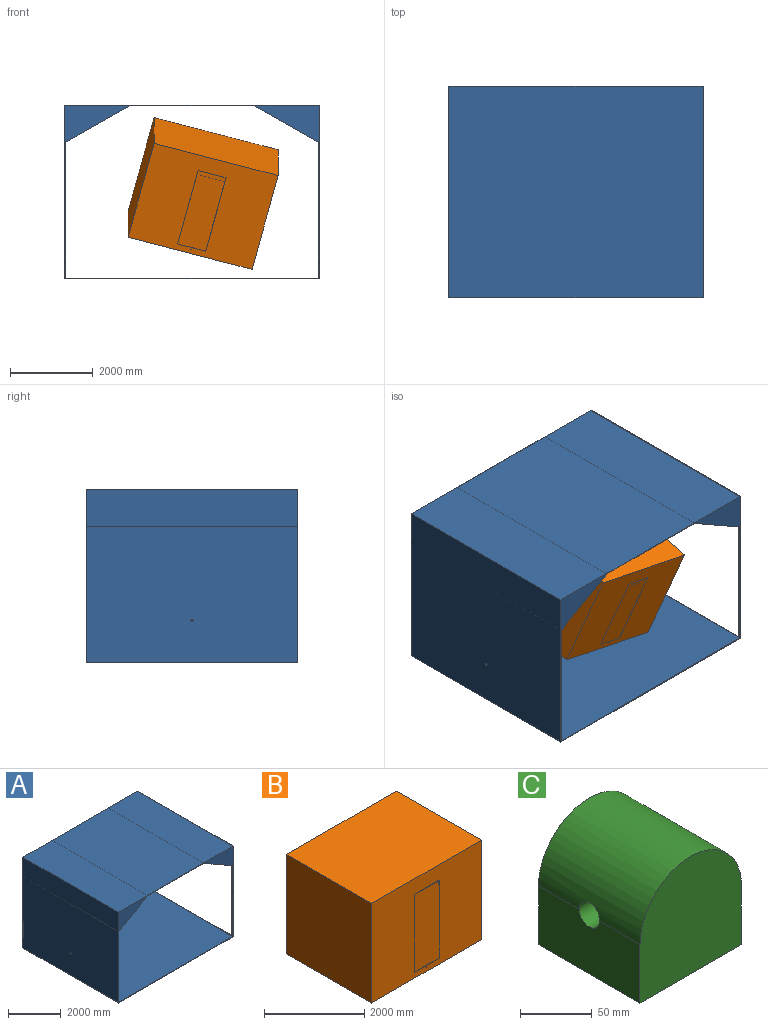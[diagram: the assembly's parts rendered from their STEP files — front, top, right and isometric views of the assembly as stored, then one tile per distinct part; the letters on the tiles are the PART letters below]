
ASSEMBLY  parts=3 mates=2
PART A: 20 faces, bbox 6140x5100x4200 mm
  f0: plane 5100x3000mm, normal (0,0,-1), area 15300000mm2, adj f10,f11,f17,f19
  f1: plane 3280x55mm, normal (-1,0,0), area 180400mm2, adj f7,f10,f12,f19
  f2: plane 5100x4200mm, normal (1,0,0), area 656610mm2, adj f3,f5,f9,f10,f11,f12,f13,f16
  f3: plane 6140x5100mm, normal (0,0,1), area 31314000mm2, adj f2,f4,f10,f11
  f4: plane 5100x4200mm, normal (-1,0,0), area 21418036.5mm2, adj f3,f9,f10,f11,f14
  f5: plane 4990x20mm, normal (0,0,-1), area 99800mm2, adj f2,f12,f13,f18
  f6: plane 3280x55mm, normal (-1,0,0), area 180400mm2, adj f7,f11,f13,f19
  f7: plane 6100x5100mm, normal (0,0,1), area 31110000mm2, adj f1,f6,f8,f10,f11,f15
  f8: plane 5100x3280mm, normal (1,0,0), area 16726036.5mm2, adj f7,f10,f11,f14,f17
  f9: plane 6140x5100mm, normal (0,0,-1), area 31314000mm2, adj f2,f4,f10,f11
  f10: plane 6140x4200mm, normal (0,-1,0), area 1776000mm2, adj f0,f1,f2,f3,f4,f7,f8,f9
  f11: plane 6140x4200mm, normal (0,1,0), area 1776000mm2, adj f0,f2,f3,f4,f6,f7,f8,f9
  f12: plane 4161x20mm, normal (0,1,0), area 83220mm2, adj f1,f2,f5,f15,f16,f18
  f13: plane 4161x20mm, normal (0,-1,0), area 83220mm2, adj f2,f5,f6,f15,f16,f18
  f14: cylinder r=25mm len=50mm, axis (1,0,0), area 3141.6mm2, adj f4,f8
  f15: plane 4990x1mm, normal (1,0,0), area 4990mm2, adj f7,f12,f13,f16
  f16: plane 4990x20mm, normal (0,0,1), area 99800mm2, adj f2,f12,f13,f15
  f17: plane 5100x1550mm, normal (0.49,0,-0.87), area 9090168.8mm2, adj f0,f8,f10,f11
  f18: plane 4990x880mm, normal (1,0,0), area 4391200mm2, adj f5,f12,f13,f19
  f19: plane 5100x1550mm, normal (-0.49,0,-0.87), area 9090168.8mm2, adj f0,f1,f6,f10,f11,f18
PART B: 68 faces, bbox 3100x2406.1x2445 mm
  f0: plane 700x20mm, normal (0,0,1), area 2139.3mm2, adj f1,f61,f62,f63,f65
  f1: plane 3100x2430mm, normal (0,-1,0), area 6202770.4mm2, adj f0,f2,f21,f22,f23,f24,f55,f61
  f2: plane 700x20mm, normal (0,0,-1), area 2139.3mm2, adj f1,f61,f62,f63,f65
  f3: plane 754.5x754.5mm, normal (0,0,-1), area 493317.8mm2, adj f12,f26,f29,f39,f40,f41,f42,f54
  f4: plane 754.5x754.5mm, normal (0,0,-1), area 527455.2mm2, adj f5,f7,f9,f12,f14,f15,f26,f27
  f5: cylinder r=7.5mm len=11.36mm, axis (0,0,-1), area 12.7mm2, adj f4,f6,f55
  f6: plane 11.36x2.6mm, normal (0,0,-1), area 20.5mm2, adj f5,f55
  f7: plane 195.1x1mm, normal (0,1,0), area 195mm2, adj f4,f10,f32,f55
  f8: cylinder r=7.5mm len=11.36mm, axis (0,0,-1), area 12.7mm2, adj f10,f11,f55
  f9: plane 195.1x1mm, normal (0,-1,0), area 195mm2, adj f4,f10,f32,f55
  f10: plane 200x195.1mm, normal (0,0,-1), area 38999.7mm2, adj f7,f8,f9,f32,f55
  f11: plane 11.18x2.5mm, normal (0,0,-1), area 19.4mm2, adj f8,f55
  f12: cylinder r=5mm len=1550mm, axis (-1,0,0), area 36462.4mm2, adj f3,f4,f14,f15,f16,f21,f26,f39
  f13: plane 754.5x754.5mm, normal (0,0,-1), area 493317.8mm2, adj f17,f28,f29,f45,f47,f48,f53,f54
  f14: plane 85.4x49.31mm, normal (-0.5,0.87,0), area 98.5mm2, adj f4,f12,f15,f44
  f15: plane 49.31x28.47mm, normal (0.87,0.5,0), area 56.9mm2, adj f4,f12,f14,f44
  f16: plane 387.31x373.21mm, normal (0,0,-1), area 75789.6mm2, adj f12,f39,f40,f41,f42,f43
  f17: plane 287.31x165.88mm, normal (-0.87,0.5,0), area 331.7mm2, adj f13,f19,f45,f53
  f18: plane 85.4x49.31mm, normal (0.5,0.87,0), area 98.5mm2, adj f20,f46,f50,f53
  f19: plane 387.31x373.21mm, normal (0,0,-1), area 75789.6mm2, adj f17,f45,f47,f48,f49,f53
  f20: plane 754.5x754.5mm, normal (0,0,-1), area 527455.2mm2, adj f18,f27,f28,f30,f33,f34,f36,f46
  f21: plane 2430x2400mm, normal (1,0,0), area 5831921.5mm2, adj f1,f12,f22,f24,f25
  f22: plane 3100x2400mm, normal (0,0,1), area 7440000mm2, adj f1,f21,f23,f25
  f23: plane 2430x2400mm, normal (-1,0,0), area 5831921.5mm2, adj f1,f22,f24,f25,f53
  f24: plane 3100x2400mm, normal (0,0,-1), area 4485039mm2, adj f1,f21,f23,f25,f56,f57,f58,f59
  f25: plane 3100x2430mm, normal (0,1,0), area 7532921.5mm2, adj f21,f22,f23,f24,f54
  f26: plane 1519x115mm, normal (-1,0,0), area 174645.7mm2, adj f3,f4,f12,f27,f29,f60
  f27: plane 1519x115mm, normal (0,1,0), area 174645.7mm2, adj f4,f20,f26,f28,f55,f60
  f28: plane 1519x115mm, normal (1,0,0), area 174645.7mm2, adj f13,f20,f27,f29,f53,f60
  f29: plane 1519x115mm, normal (0,-1,0), area 174645.7mm2, adj f3,f13,f26,f28,f54,f60
  f30: cylinder r=7.5mm len=11.36mm, axis (0,0,-1), area 12.7mm2, adj f20,f31,f55
  f31: plane 11.36x2.6mm, normal (0,0,-1), area 20.5mm2, adj f30,f55
  f32: plane 200x1mm, normal (-1,0,0), area 200mm2, adj f4,f7,f9,f10
  f33: plane 195.1x1mm, normal (0,1,0), area 195mm2, adj f20,f34,f37,f55
  f34: plane 200x1mm, normal (1,0,0), area 200mm2, adj f20,f33,f36,f37
  f35: cylinder r=7.5mm len=11.36mm, axis (0,0,-1), area 12.7mm2, adj f37,f38,f55
  f36: plane 195.1x1mm, normal (0,-1,0), area 195mm2, adj f20,f34,f37,f55
  f37: plane 200x195.1mm, normal (0,0,-1), area 38999.7mm2, adj f33,f34,f35,f36,f55
  f38: plane 11.18x2.5mm, normal (0,0,-1), area 19.4mm2, adj f35,f55
  f39: plane 70.83x40.9mm, normal (-0.5,0.87,0), area 81.7mm2, adj f3,f12,f16,f42
  f40: plane 287.31x165.88mm, normal (0.87,0.5,0), area 331.7mm2, adj f3,f12,f16,f41
  f41: plane 173.21x100mm, normal (0.5,-0.87,0), area 200mm2, adj f3,f16,f40,f42
  f42: plane 346.41x200mm, normal (-0.87,-0.5,0), area 400mm2, adj f3,f16,f39,f41
  f43: cylinder r=7.5mm len=15mm, axis (0,0,-1), area 47.1mm2, adj f16,f51
  f44: plane 113.87x49.31mm, normal (0,0,-1), area 2807.2mm2, adj f12,f14,f15
  f45: plane 173.21x100mm, normal (-0.5,-0.87,0), area 200mm2, adj f13,f17,f19,f48
  f46: plane 49.31x28.47mm, normal (-0.87,0.5,0), area 56.9mm2, adj f18,f20,f50,f53
  f47: plane 70.83x40.9mm, normal (0.5,0.87,0), area 81.7mm2, adj f13,f19,f48,f53
  f48: plane 346.41x200mm, normal (0.87,-0.5,0), area 400mm2, adj f13,f19,f45,f47
  f49: cylinder r=7.5mm len=15mm, axis (0,0,-1), area 47.1mm2, adj f19,f52
  f50: plane 113.87x49.31mm, normal (0,0,-1), area 2807.2mm2, adj f18,f46,f53
  f51: plane 15x15mm, normal (0,0,-1), area 176.7mm2, adj f43
  f52: plane 15x15mm, normal (0,0,-1), area 176.7mm2, adj f49
  f53: cylinder r=5mm len=1550mm, axis (-1,0,0), area 36462.4mm2, adj f13,f17,f18,f19,f20,f23,f28,f46
  f54: cylinder r=5mm len=1200mm, axis (0,-1,0), area 25718.9mm2, adj f3,f12,f13,f25,f29,f53
  f55: cylinder r=5mm len=1200mm, axis (0,-1,0), area 25316.2mm2, adj f1,f4,f5,f6,f7,f8,f9,f10
  f56: plane 1719x15mm, normal (-1,0,0), area 25785mm2, adj f24,f57,f59,f60
  f57: plane 1719x15mm, normal (0,1,0), area 25785mm2, adj f24,f56,f58,f60
  f58: plane 1719x15mm, normal (1,0,0), area 25785mm2, adj f24,f57,f59,f60
  f59: plane 1719x15mm, normal (0,-1,0), area 25785mm2, adj f24,f56,f58,f60
  f60: plane 1719x1719mm, normal (0,0,-1), area 647600mm2, adj f26,f27,f28,f29,f56,f57,f58,f59
  f61: plane 1800x20mm, normal (-1,0,0), area 36000mm2, adj f0,f1,f2,f62
  f62: plane 1800x700mm, normal (0,-1,0), area 1260000mm2, adj f0,f2,f61,f63
  f63: plane 1800x699.97mm, normal (0.01,1,0), area 1260000mm2, adj f0,f2,f62,f65
  f64: plane 1900x699.89mm, normal (-0.01,-1,0), area 1329834.2mm2, adj f1,f65,f66,f67
  f65: plane 1900x20mm, normal (1,-0.01,0), area 36610.8mm2, adj f0,f1,f2,f63,f64,f66,f67
  f66: plane 699.94x6.11mm, normal (0,0,1), area 2137.5mm2, adj f1,f64,f65
  f67: plane 699.94x6.11mm, normal (0,0,-1), area 2137.5mm2, adj f1,f64,f65
PART C: 7 faces, bbox 100x100x100 mm
  f0: plane 100x50mm, normal (-1,0,0), area 4842.9mm2, adj f1,f2,f4,f5,f6
  f1: cylinder r=50mm len=100mm, axis (0,1,0), area 15392.2mm2, adj f0,f3,f4,f5,f6
  f2: plane 100x100mm, normal (0,0,-1), area 10000mm2, adj f0,f3,f4,f5
  f3: plane 100x50mm, normal (1,0,0), area 4842.9mm2, adj f1,f2,f4,f5,f6
  f4: plane 100x100mm, normal (0,-1,0), area 8927mm2, adj f0,f1,f2,f3
  f5: plane 100x100mm, normal (0,1,0), area 8927mm2, adj f0,f1,f2,f3
  f6: cylinder r=10mm len=100mm, axis (-1,0,0), area 6251.5mm2, adj f0,f1,f3
PLACE A at identity fixed
PLACE B rot(axis=(0.7,0.7,0.09),21.2deg) t=(268.58,-1662.68,272.76)mm
PLACE C rot(axis=(1,0,0),15deg) t=(-20,-2501.7,-1067.06)mm
MATE revolute A.f14 <-> C.f6  axis (-1,0,0) through (-3070,-2550,-1080)mm
MATE revolute C.f1 <-> B.f54  axis (0,-0.97,-0.26) through (-20,-2598.3,-1092.94)mm
